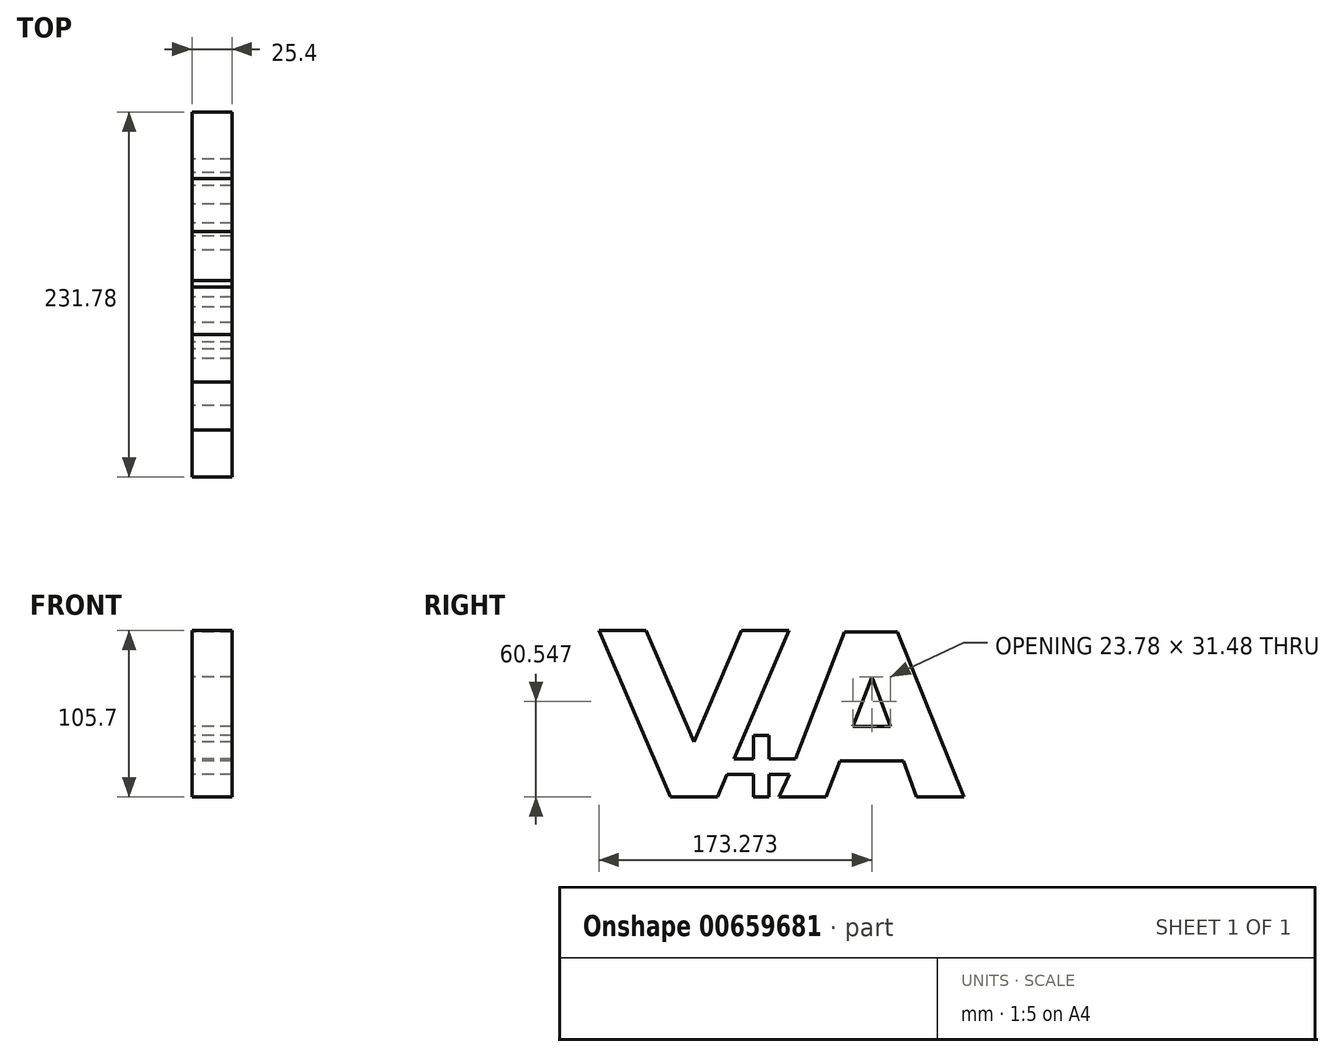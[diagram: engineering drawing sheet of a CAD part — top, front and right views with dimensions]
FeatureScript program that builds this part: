
annotation { "Feature Type Name" : "Feature", "Feature Type Description" : "" }
export const myFeature = defineFeature(function(context is Context, id is Id, definition is map)
    precondition{}
    {
        {
            var Q0;
            Q0=qCreatedBy(makeId("Right.planeOp"),FACE);
            var sketch = newSketch(context, id + "F0", { "sketchPlane" : qUnion([Q0])});
            skLineSegment(sketch, "E0", {"start": v(0, 0) * mm, "end": v(-15, 0) * mm});
            skLineSegment(sketch, "E1", {"start": v(-15, 0) * mm, "end": v(-60.3, 105.7) * mm});
            skLineSegment(sketch, "E2", {"start": v(-60.3, 105.7) * mm, "end": v(-30.3, 105.7) * mm});
            skLineSegment(sketch, "E3", {"start": v(-30.3, 105.7) * mm, "end": v(0, 35) * mm});
            skLineSegment(sketch, "E4", {"start": v(0, 0) * mm, "end": v(0, 35) * mm});
            skLineSegment(sketch, "E5.MirrorCS", {"start": v(30.3, 105.7) * mm, "end": v(0, 35) * mm});
            skLineSegment(sketch, "E6.MirrorCS", {"start": v(60.3, 105.7) * mm, "end": v(30.3, 105.7) * mm});
            skLineSegment(sketch, "E7.MirrorCS", {"start": v(15, 0) * mm, "end": v(60.3, 105.7) * mm});
            skLineSegment(sketch, "E8.MirrorCS", {"start": v(0, 0) * mm, "end": v(15, 0) * mm});
            skLineSegment(sketch, "E9", {"start": v(21.1, 14.23) * mm, "end": v(60.7, 14.23) * mm});
            skLineSegment(sketch, "E10", {"start": v(25.38, 24.23) * mm, "end": v(60.38, 24.23) * mm});
            skLineSegment(sketch, "E11", {"start": v(37.72, 24.23) * mm, "end": v(37.72, 39.2) * mm});
            skLineSegment(sketch, "E12", {"start": v(37.72, 39.2) * mm, "end": v(47.72, 39.2) * mm});
            skLineSegment(sketch, "E13", {"start": v(47.72, 39.2) * mm, "end": v(47.72, 24.23) * mm});
            skLineSegment(sketch, "E14", {"start": v(37.72, 14.23) * mm, "end": v(37.72, 3.9) * mm});
            skLineSegment(sketch, "E15", {"start": v(37.72, 14.23) * mm, "end": v(37.72, 0) * mm});
            skLineSegment(sketch, "E16", {"start": v(47.72, 14.23) * mm, "end": v(47.72, 0) * mm});
            skLineSegment(sketch, "E17", {"start": v(37.72, 0) * mm, "end": v(47.72, 0) * mm});
            skLineSegment(sketch, "E18", {"start": v(60.7, 14.23) * mm, "end": v(95.5, 104.79) * mm});
            skLineSegment(sketch, "E19", {"start": v(95.5, 104.79) * mm, "end": v(129.18, 104.79) * mm});
            skLineSegment(sketch, "E20", {"start": v(60.7, 14.23) * mm, "end": v(53.87, 0) * mm});
            skLineSegment(sketch, "E21", {"start": v(53.87, 0) * mm, "end": v(83.87, 0) * mm});
            skLineSegment(sketch, "E22", {"start": v(83.87, 0) * mm, "end": v(113.18, 76.29) * mm});
            skLineSegment(sketch, "E23", {"start": v(113.18, 76.29) * mm, "end": v(141.48, 0) * mm});
            skLineSegment(sketch, "E24", {"start": v(141.48, 0) * mm, "end": v(171.48, 0) * mm});
            skLineSegment(sketch, "E25", {"start": v(129.18, 104.79) * mm, "end": v(171.48, 0) * mm});
            skLineSegment(sketch, "E26", {"start": v(60.38, 24.23) * mm, "end": v(64.54, 24.23) * mm});
            skLineSegment(sketch, "E27", {"start": v(101.09, 44.8) * mm, "end": v(124.86, 44.8) * mm});
            skLineSegment(sketch, "E28", {"start": v(92.6, 22.72) * mm, "end": v(133.05, 22.72) * mm});
            skSolve(sketch);
        }
        {
            var Q0;
            Q0 = qSketchRegion(id + "F0", true);
            extrude(context, id + "F1", {"entities" : qUnion([Q0]), "depth" : 25.4 * mm, "offsetDistance" : 25.4 * mm});
        }
    });
